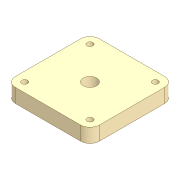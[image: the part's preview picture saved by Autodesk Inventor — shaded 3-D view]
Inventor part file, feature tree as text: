
AUTODESK INVENTOR PART (.ipt)
format: ipt  version: 2020 (Build 240168000, 168)  size: 112,640 bytes
history: native  units: mm
features: mirror x2, other x1, extrude x1, sketch x1
ambient origin geometry x8: Origin, YZ Plane, XZ Plane, XY Plane, X Axis, Y Axis, Z Axis, Center Point
bodies: Body1 (feature_tree)
feature tree (5):
  other  "Sólido1"
  extrude  "Extrusão1"  Depth=36.0mm
  mirror  "Espelhamento1"
  mirror  "Espelhamento2"
  sketch  "Esboço1"  dims[d0=11.6mm d1=36.0mm d2=36.0mm d3=8.0mm d4=5.0mm d5=12.0mm d6=0.0mm d7=8.0mm d8=8.0mm]
